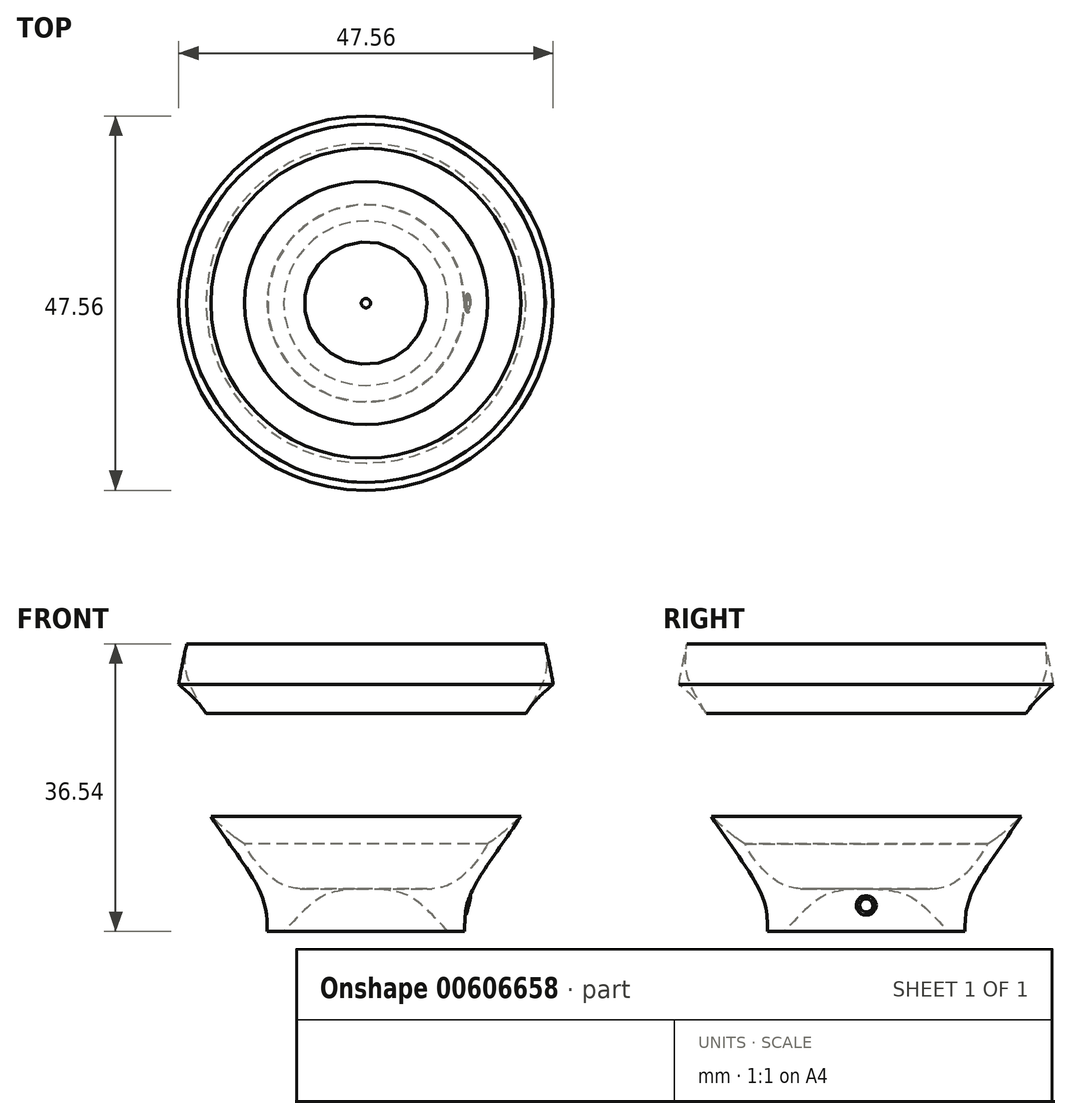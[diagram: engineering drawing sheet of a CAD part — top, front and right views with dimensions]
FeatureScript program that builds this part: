
annotation { "Feature Type Name" : "Feature", "Feature Type Description" : "" }
export const myFeature = defineFeature(function(context is Context, id is Id, definition is map)
    precondition{}
    {
        {
            var Q0;
            Q0=qCreatedBy(makeId("Front.planeOp"),FACE);
            var sketch = newSketch(context, id + "F0", { "sketchPlane" : qUnion([Q0])});
            skFitSpline(sketch, "E0", {"points": [v(22.76, 15.34) * mm, v(23.16, 0) * mm, v(13.63, -15.75) * mm, v(12.55, -21.2) * mm], "startDerivative": vector(9.06, -41) * mm, "endDerivative": vector(0.14, -22.25) * mm});
            skFitSpline(sketch, "E1", {"points": [v(22.76, 15.34) * mm, v(22.76, 11.46) * mm, v(20.3, 6.5) * mm], "startDerivative": vector(1.03, -8.37) * mm, "endDerivative": vector(-5.74, -9.28) * mm});
            skLineSegment(sketch, "E2", {"start": v(12.55, -21.2) * mm, "end": v(10.45, -21.2) * mm});
            skFitSpline(sketch, "E3", {"points": [v(16.76, -6.2) * mm, v(14.92, -11) * mm, v(10.82, -15.14) * mm, v(7.78, -15.75) * mm], "startDerivative": vector(-3.73, -13.6) * mm, "endDerivative": vector(-10.87, 0.28) * mm});
            skFitSpline(sketch, "E4.trimOffspring", {"points": [v(23.88, 10.28) * mm, v(20.3, 6.5) * mm, v(17.36, -1.85) * mm, v(16.4, -11.2) * mm], "startDerivative": vector(-13.83, -11.68) * mm, "endDerivative": vector(-1.4, -25.2) * mm});
            skLineSegment(sketch, "E5", {"start": v(0, 14.64) * mm, "end": v(0, -2.67) * mm, "construction": true});
            skLineSegment(sketch, "E6", {"start": v(8.37, -15.75) * mm, "end": v(0.6, -15.75) * mm});
            skFitSpline(sketch, "E7", {"points": [v(10.45, -21.2) * mm, v(7.99, -18.67) * mm, v(5.11, -16.54) * mm, v(0.6, -15.75) * mm], "startDerivative": vector(-7.64, 8.04) * mm, "endDerivative": vector(-13.37, 1) * mm});
            skFitSpline(sketch, "E8", {"points": [v(19.68, -6.6) * mm, v(16.96, -8.99) * mm, v(15.43, -10.05) * mm], "startDerivative": vector(-4.96, -4.56) * mm, "endDerivative": vector(-3.45, -2.22) * mm});
            skSolve(sketch);
        }
        {
            var Q0;
            {var subQ4=sQuery(id+"F0.wireOp",EDGE,"E2");Q0=makeQuery(id+"F0.imprint","IMPRINT",FACE,{"disambiguationData":[TD([[makeQuery(id+"F0.imprint","IMPRINT",EDGE,{"derivedFrom":subQ4}),-1.0]])]});}
            var Q1;
            {var subQ3=sQuery(id+"F0.wireOp",EDGE,"E1");Q1=makeQuery(id+"F0.imprint","IMPRINT",FACE,{"disambiguationData":[TD([[makeQuery(id+"F0.imprint","IMPRINT",EDGE,{"derivedFrom":subQ3}),1.0]])]});}
            var Q2;
            Q2=sQuery(id+"F0.wireOp",EDGE,"E5");
            revolve(context, id + "F1", {"entities" : qUnion([Q0, Q1]), "axis" : qUnion([Q2]), "revolveType" : RevolveType.FULL});
        }
        {
            var Q0;
            Q0=qCreatedBy(makeId("Front.planeOp"),FACE);
            var sketch = newSketch(context, id + "F2", { "sketchPlane" : qUnion([Q0])});
            skLineSegment(sketch, "E9", {"start": v(13.24, -16.66) * mm, "end": v(12.63, -19.1) * mm});
            skLineSegment(sketch, "E10", {"start": v(13.72, -18.08) * mm, "end": v(12.16, -17.7) * mm});
            skFitSpline(sketch, "E11", {"points": [v(12.63, -19.1) * mm, v(12.32, -18.05) * mm, v(12.34, -17.73) * mm], "startDerivative": vector(-0.73, 1.4) * mm, "endDerivative": vector(0.15, 0.75) * mm});
            skFitSpline(sketch, "E12", {"points": [v(12.5, -17.77) * mm, v(12.48, -18.25) * mm, v(12.73, -18.7) * mm], "startDerivative": vector(-0.16, -0.99) * mm, "endDerivative": vector(0.63, -0.88) * mm});
            skFitSpline(sketch, "E13", {"points": [v(12.73, -18.7) * mm, v(12.8, -18.94) * mm, v(12.63, -19.1) * mm], "startDerivative": vector(0.24, -0.5) * mm, "endDerivative": vector(-0.44, -0.31) * mm});
            skSolve(sketch);
        }
        {
            var Q0;
            Q0 = qSketchRegion(id + "F2", true);
            var Q1;
            Q1=sQuery(id+"F2.wireOp",EDGE,"E10");
            revolve(context, id + "F3", {"operationType" : NewBodyOperationType.ADD, "entities" : qUnion([Q0]), "axis" : qUnion([Q1]), "revolveType" : RevolveType.FULL});
        }
    });
